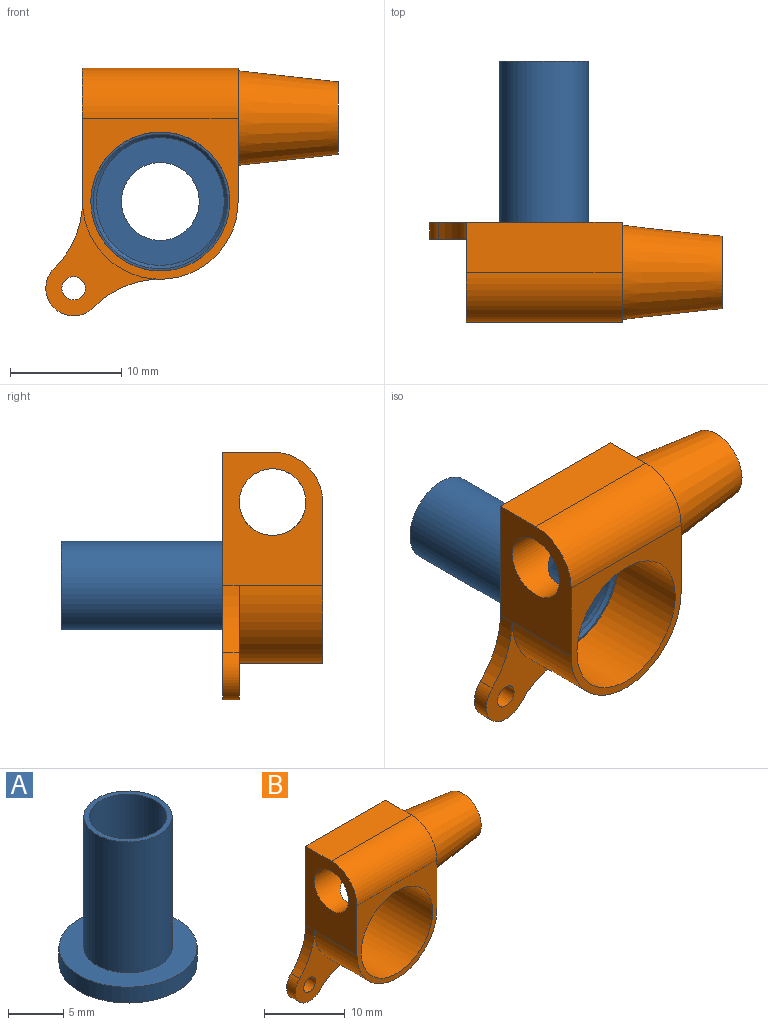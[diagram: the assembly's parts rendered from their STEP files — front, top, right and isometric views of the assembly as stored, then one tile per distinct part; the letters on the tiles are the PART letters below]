
ASSEMBLY  parts=2 mates=1
PART A: 9 faces, bbox 12.5x12.5x16.3 mm
  f0: cylinder r=6.25mm len=12.5mm, axis (0,0,-1), area 68.7mm2, adj f1,f3
  f1: plane 12.5x12.5mm, normal (0,0,1), area 72.5mm2, adj f0,f5
  f2: cylinder r=5.75mm len=11.5mm, axis (0,0,1), area 16.3mm2, adj f4,f8
  f3: plane 12.5x12.5mm, normal (0,0,-1), area 7.7mm2, adj f0,f8
  f4: plane 11.5x11.5mm, normal (0,0,-1), area 65.4mm2, adj f2,f7
  f5: cylinder r=4mm len=14.5mm, axis (0,0,-1), area 364.4mm2, adj f1,f6
  f6: plane 8x8mm, normal (0,0,1), area 11.8mm2, adj f5,f7
  f7: cylinder r=3.5mm len=15.5mm, axis (0,0,1), area 340.9mm2, adj f4,f6
  f8: cone r=5.75mm half-angle=45deg, axis (0,0,-1), area 15.7mm2, adj f2,f3
PART B: 16 faces, bbox 26.3x9x22.3 mm
  f0: cylinder r=7mm len=14mm, axis (0,1,0), area 181.4mm2, adj f1,f4,f5,f6,f13,f15
  f1: plane 12x9mm, normal (1,0,0), area 46.9mm2, adj f0,f2,f5,f6,f7,f10
  f2: plane 14x4.5mm, normal (0,0,1), area 63mm2, adj f1,f4,f6,f7
  f3: cylinder r=6.25mm len=12.5mm, axis (0,1,0), area 310.6mm2, adj f5,f6,f9
  f4: plane 12x9mm, normal (-1,0,0), area 75.4mm2, adj f0,f2,f5,f6,f7,f9,f11
  f5: plane 14.5x14mm, normal (0,-1,0), area 59.3mm2, adj f0,f1,f3,f4,f7
  f6: plane 22.3x17.3mm, normal (0,1,0), area 154mm2, adj f0,f1,f2,f3,f4,f11,f12,f13
  f7: cylinder r=4.5mm len=14mm, axis (1,0,0), area 99mm2, adj f1,f2,f4,f5
  f8: plane 6.5x6.5mm, normal (1,0,0), area 4.9mm2, adj f9,f10
  f9: cylinder r=3mm len=23mm, axis (1,0,0), area 386.6mm2, adj f3,f4,f8
  f10: cone r=3.25mm half-angle=6.3deg, axis (-1,0,0), area 213.4mm2, adj f1,f8
  f11: cylinder r=8.37mm len=6.01mm, axis (0,1,0), area 10mm2, adj f4,f6,f12,f15
  f12: cylinder r=2.5mm len=4.29mm, axis (0,1,0), area 11.9mm2, adj f6,f11,f13,f15
  f13: cylinder r=8.37mm len=6.01mm, axis (0,1,0), area 10mm2, adj f0,f6,f12,f15
  f14: cylinder r=1.05mm len=2.1mm, axis (0,1,0), area 9.9mm2, adj f6,f15
  f15: plane 10.3x10.3mm, normal (0,-1,0), area 31.8mm2, adj f0,f11,f12,f13,f14
PLACE A rot(axis=(-1,0,0),90deg) t=(6.89,2.38,1.8)mm
PLACE B t=(6.89,3.38,1.8)mm
MATE fastened A.f0 <-> B.f3  axis (0,1,0) through (6.89,3.38,1.8)mm
